# Revit family: 71257CHN_NEW
name_source: partatom
category: Plumbing Fixtures
revit_build: Autodesk Revit 2018 (Build: 20170223_1515(x64)
units: mm (PartAtom-declared; Revit-internal decimal feet)

## family parameters
Cut with Voids When Loaded = Yes
Host = Face
OmniClass Number = 23.31.11.00
OmniClass Title = Faucets
Part Type = Normal
Room Calculation Point = No
Round Connector Dimension = Use Diameter
Shared = No

## types (2) — shared parameters
Always visible = Yes
BIMobject category = Taps & Mixers
Connector Description = Water Inlet 9.5 mm
Date Updated = 23/06/2023
Date of publishing = 11/2/2022 12:00:00 AM
Default Elevation = 1219 mm
Description = Logis Single lever basin mixer 240 Fine with push-open waste set
Design country = Germany
Diameter = 10 mm  [stored 0.0328084 ft]
Edition number = 1
IFC Classification = Valve
Manufacturer = Hansgrohe
Manufacturer country = Germany
Manufacturer name = hansgrohe
Masterformat 2014 Code = 22 41 39
Masterformat 2014 Description = Residential Faucets, Supplies, and Trim
Model = 71257CHN
OmniClass Code = 23-31 11 00
OmniClass Description = Faucets
Product Guid = dd29779a-f295-4962-9c66-52187b6dce9b
Product SKU = 71257CHN
Product data url = https://bimobject.com
Product family = Logis
Product group = Basin mixers
Product name = Logis Single lever basin mixer 240 Fine with push-open waste set
Product url = https://www.hansgrohe.com
QR code = https://bimobject.com
UNSPSC Code = 301815
URL = https://www.hansgrohe.com
Uniclass 2015 Code = Pr_40_20_87
Uniclass 2015 Name = Taps and water supply outlet fittings
Uniformat II Code = D2010
Uniformat II Description = Plumbing Fixtures
Version = 1
Weight Net (Kg) = 3

## per-type parameters (varying)
| type | Material 1 |
| 677 Matte Black | Hansgrohe - Metal - 677 Matte Black |
| 007 Chrome | Hansgrohe - Metal - 007 Chrome |

note: [stored X ft] marks values corroborated as IEEE doubles in the binary element streams (Revit-internal decimal feet)

## geometry (parser evidence)
native form markers: Sweep x2
no freeform markers — native parametric forms only
